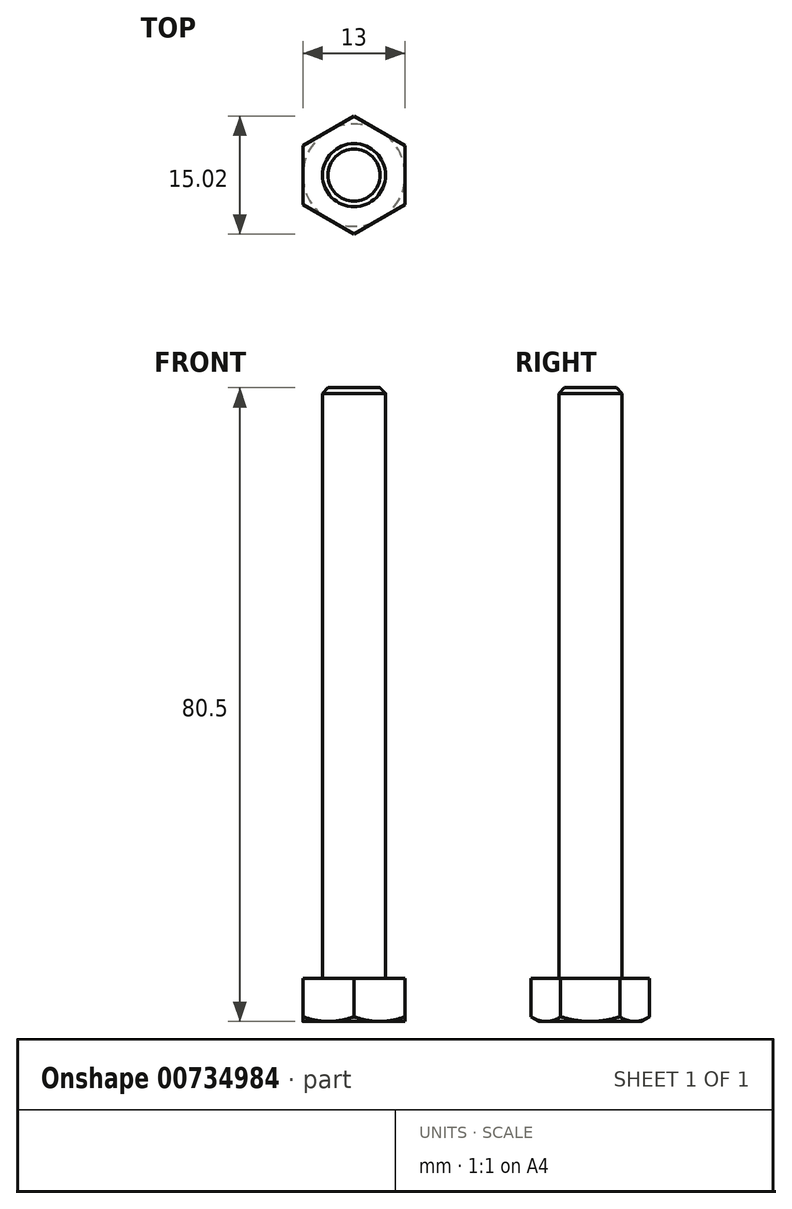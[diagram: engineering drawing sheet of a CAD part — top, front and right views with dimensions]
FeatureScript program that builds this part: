
annotation { "Feature Type Name" : "Feature", "Feature Type Description" : "" }
export const myFeature = defineFeature(function(context is Context, id is Id, definition is map)
    precondition{}
    {
        {
            var Q0;
            Q0=qCreatedBy(makeId("Top.planeOp"),FACE);
            var sketch = newSketch(context, id + "F0", { "sketchPlane" : qUnion([Q0])});
            skCircle(sketch, "E0.cCircle", {"center": v(0, 0) * mm, "radius": 6.5 * mm, "construction": true});
            skLineSegment(sketch, "E0.0", {"start": v(6.5, -3.75) * mm, "end": v(0, -7.5) * mm});
            skLineSegment(sketch, "E0.1", {"start": v(0, -7.5) * mm, "end": v(-6.5, -3.75) * mm});
            skLineSegment(sketch, "E0.2", {"start": v(-6.5, -3.75) * mm, "end": v(-6.5, 3.75) * mm});
            skLineSegment(sketch, "E0.3", {"start": v(-6.5, 3.75) * mm, "end": v(0, 7.5) * mm});
            skLineSegment(sketch, "E0.4", {"start": v(0, 7.5) * mm, "end": v(6.5, 3.75) * mm});
            skLineSegment(sketch, "E0.5", {"start": v(6.5, 3.75) * mm, "end": v(6.5, -3.75) * mm});
            skPoint(sketch, "E0.0.midPoint", {"position": v(3.25, -5.63) * mm});
            skSolve(sketch);
        }
        {
            var Q0;
            Q0 = qSketchRegion(id + "F0", true);
            extrude(context, id + "F1", {"entities" : qUnion([Q0]), "depth" : 5.5 * mm, "offsetDistance" : 25 * mm});
        }
        {
            var Q0;
            Q0=makeQuery(id+"F1.opExtrude","CAP_FACE",FACE,{"disambiguationData":[OSD([sQuery(id+"F0.wireOp",EDGE,"E0.0"),sQuery(id+"F0.wireOp",EDGE,"E0.1"),sQuery(id+"F0.wireOp",EDGE,"E0.2"),sQuery(id+"F0.wireOp",EDGE,"E0.3"),sQuery(id+"F0.wireOp",EDGE,"E0.4"),sQuery(id+"F0.wireOp",EDGE,"E0.5")])],"isStart":false});
            var sketch = newSketch(context, id + "F2", { "sketchPlane" : qUnion([Q0])});
            skCircle(sketch, "E1", {"center": v(0, 0) * mm, "radius": 4 * mm});
            skSolve(sketch);
        }
        {
            var Q0;
            Q0 = qSketchRegion(id + "F2", true);
            extrude(context, id + "F3", {"entities" : qUnion([Q0]), "operationType" : NewBodyOperationType.ADD, "depth" : 75 * mm, "offsetDistance" : 25 * mm});
        }
        {
            var Q0;
            Q0=qCreatedBy(makeId("Front.planeOp"),FACE);
            var sketch = newSketch(context, id + "F4", { "sketchPlane" : qUnion([Q0])});
            skLineSegment(sketch, "E2", {"start": v(0, 0) * mm, "end": v(0, 9.78) * mm, "construction": true});
            skLineSegment(sketch, "E3", {"start": v(6.5, 0) * mm, "end": v(11.16, 2.69) * mm});
            skLineSegment(sketch, "E4", {"start": v(11.16, 2.69) * mm, "end": v(11.16, 0) * mm});
            skLineSegment(sketch, "E5", {"start": v(11.16, 0) * mm, "end": v(6.5, 0) * mm});
            skSolve(sketch);
        }
        {
            var Q0;
            Q0 = qSketchRegion(id + "F4", true);
            var Q1;
            Q1=sQuery(id+"F4.wireOp",EDGE,"E2");
            revolve(context, id + "F5", {"operationType" : NewBodyOperationType.REMOVE, "surfaceOperationType" : NewSurfaceOperationType.NEW, "entities" : qUnion([Q0]), "axis" : qUnion([Q1]), "revolveType" : RevolveType.FULL, "oppositeDirection" : true});
        }
        {
            var Q0;
            Q0=makeQuery(id+"F3.opExtrude","CAP_EDGE",EDGE,{"disambiguationData":[OSD([sQuery(id+"F2.wireOp",EDGE,"E1")])],"isStart":false});
            chamfer(context, id + "F6", {"entities" : qUnion([Q0]), "width" : 0.7 * mm, "tangentPropagation" : true});
        }
    });
